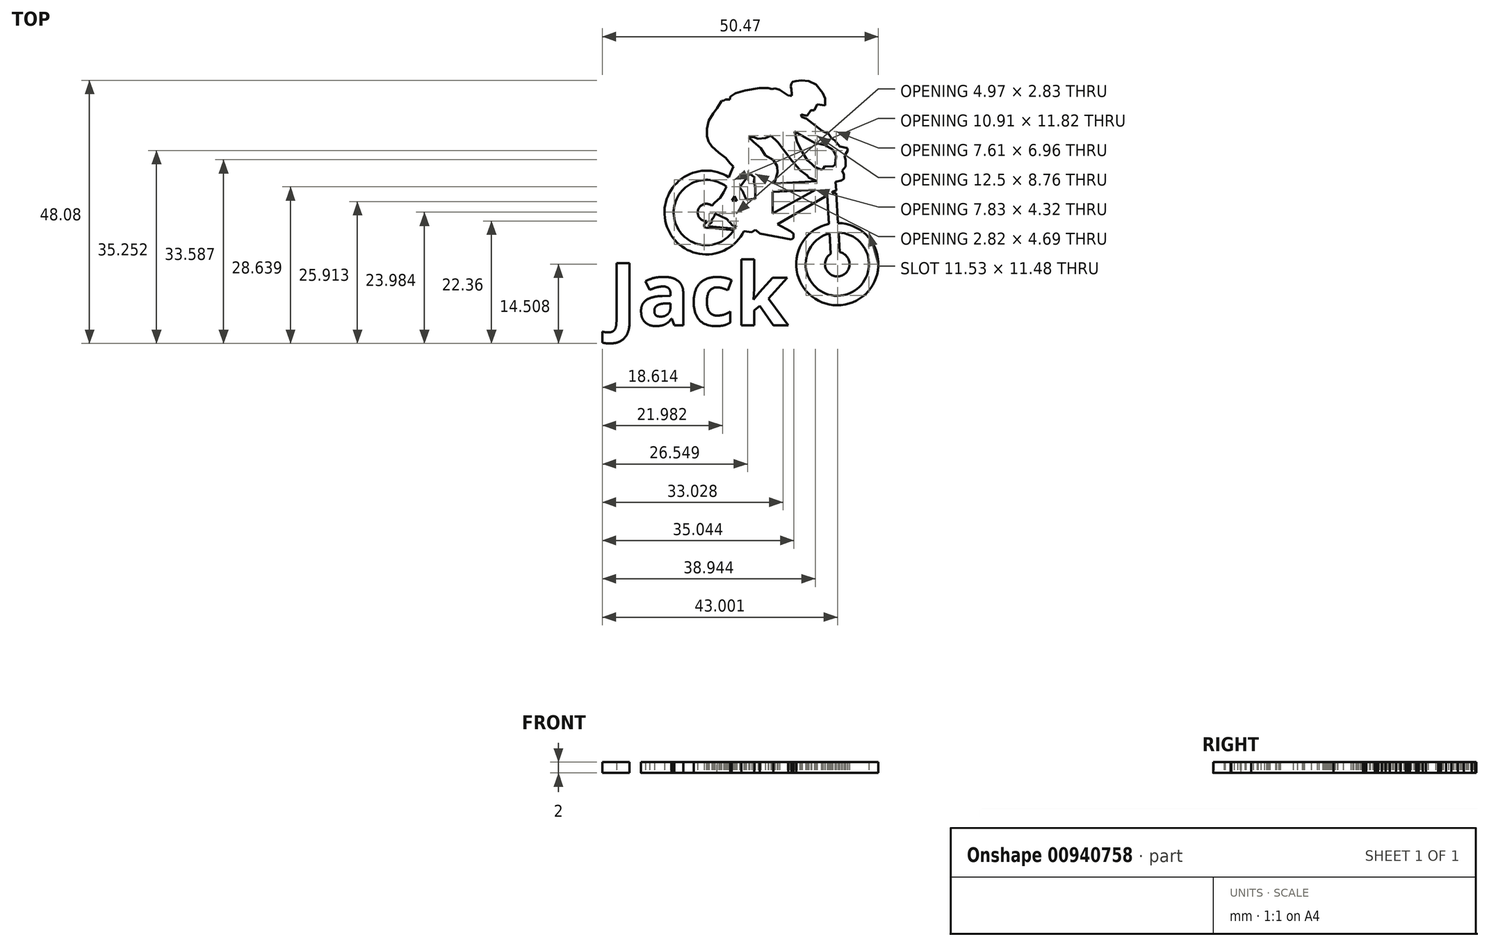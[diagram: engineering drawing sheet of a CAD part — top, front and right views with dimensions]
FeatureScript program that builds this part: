
annotation { "Feature Type Name" : "Feature", "Feature Type Description" : "" }
export const myFeature = defineFeature(function(context is Context, id is Id, definition is map)
    precondition{}
    {
        {
            var Q0;
            Q0=qCreatedBy(makeId("Top.planeOp"),FACE);
            var sketch = newSketch(context, id + "F0", { "sketchPlane" : qUnion([Q0])});
            skArc(sketch, "E0", {"start": v(9.46, 16.17) * mm, "mid": v(9.86, 16.65) * mm, "end": v(10.04, 17.25) * mm});
            skArc(sketch, "E1", {"start": v(31.19, 9.87) * mm, "mid": v(32.78, 5.77) * mm, "end": v(32.82, 10.17) * mm});
            skArc(sketch, "E2", {"start": v(13.63, 14.42) * mm, "mid": v(13.76, 14.68) * mm, "end": v(13.89, 14.94) * mm});
            skArc(sketch, "E3", {"start": v(15.74, 19.77) * mm, "mid": v(0.82, 17.96) * mm, "end": v(15.32, 14.02) * mm});
            skArc(sketch, "E4", {"start": v(30.96, 13.58) * mm, "mid": v(32.98, 2.22) * mm, "end": v(32.6, 13.75) * mm});
            skArc(sketch, "E5", {"start": v(30.86, 15.33) * mm, "mid": v(33.08, 0.5) * mm, "end": v(32.5, 15.49) * mm});
            skLineSegment(sketch, "E6", {"start": v(32.82, 10.17) * mm, "end": v(32.6, 13.75) * mm});
            skLineSegment(sketch, "E7", {"start": v(31.19, 9.87) * mm, "end": v(30.96, 13.58) * mm});
            skLineSegment(sketch, "E8", {"start": v(32.17, 20.9) * mm, "end": v(31.44, 21) * mm});
            skLineSegment(sketch, "E9", {"start": v(31.44, 21) * mm, "end": v(31.46, 21.25) * mm});
            skLineSegment(sketch, "E10", {"start": v(31.46, 21.25) * mm, "end": v(32.17, 21.42) * mm});
            skLineSegment(sketch, "E11", {"start": v(32.17, 21.42) * mm, "end": v(32.07, 23.05) * mm});
            skLineSegment(sketch, "E12", {"start": v(32.07, 23.05) * mm, "end": v(33.13, 23.28) * mm});
            skLineSegment(sketch, "E13", {"start": v(33.13, 23.28) * mm, "end": v(33.58, 23.61) * mm});
            skLineSegment(sketch, "E14", {"start": v(33.58, 23.61) * mm, "end": v(33.58, 24.32) * mm});
            skLineSegment(sketch, "E15", {"start": v(33.58, 24.32) * mm, "end": v(33.27, 25.03) * mm});
            skLineSegment(sketch, "E16", {"start": v(33.27, 25.03) * mm, "end": v(33.92, 25.8) * mm});
            skLineSegment(sketch, "E17", {"start": v(33.92, 25.8) * mm, "end": v(33.92, 26.93) * mm});
            skLineSegment(sketch, "E18", {"start": v(33.92, 26.93) * mm, "end": v(33.73, 27.75) * mm});
            skLineSegment(sketch, "E19", {"start": v(33.73, 27.75) * mm, "end": v(34.26, 28.72) * mm});
            skLineSegment(sketch, "E20", {"start": v(34.26, 28.72) * mm, "end": v(34.2, 29.16) * mm});
            skLineSegment(sketch, "E21", {"start": v(34.2, 29.16) * mm, "end": v(32.8, 29.47) * mm});
            skLineSegment(sketch, "E22", {"start": v(32.8, 29.47) * mm, "end": v(31.94, 30.57) * mm});
            skLineSegment(sketch, "E23", {"start": v(31.94, 30.57) * mm, "end": v(31.27, 31.04) * mm});
            skLineSegment(sketch, "E24", {"start": v(31.27, 31.04) * mm, "end": v(30.78, 31.8) * mm});
            skLineSegment(sketch, "E25", {"start": v(30.78, 31.8) * mm, "end": v(29.59, 32.36) * mm});
            skLineSegment(sketch, "E26", {"start": v(29.59, 32.36) * mm, "end": v(26.7, 34.6) * mm});
            skLineSegment(sketch, "E27", {"start": v(25.76, 35.35) * mm, "end": v(26.88, 35.1) * mm});
            skLineSegment(sketch, "E28", {"start": v(26.88, 35.1) * mm, "end": v(27.53, 36.08) * mm});
            skLineSegment(sketch, "E29", {"start": v(27.53, 36.08) * mm, "end": v(28.17, 36.08) * mm});
            skLineSegment(sketch, "E30", {"start": v(28.17, 36.08) * mm, "end": v(28.69, 37.17) * mm});
            skLineSegment(sketch, "E31", {"start": v(28.69, 37.17) * mm, "end": v(30.13, 37) * mm});
            skLineSegment(sketch, "E32", {"start": v(30.13, 37) * mm, "end": v(30.13, 38.23) * mm});
            skLineSegment(sketch, "E33", {"start": v(30.13, 38.23) * mm, "end": v(29.7, 39.27) * mm});
            skLineSegment(sketch, "E34", {"start": v(29.7, 39.27) * mm, "end": v(28.48, 40.78) * mm});
            skLineSegment(sketch, "E35", {"start": v(28.48, 40.78) * mm, "end": v(27.15, 41.4) * mm});
            skLineSegment(sketch, "E36", {"start": v(27.15, 41.4) * mm, "end": v(25.85, 41.56) * mm});
            skLineSegment(sketch, "E37", {"start": v(25.85, 41.56) * mm, "end": v(24.83, 41.42) * mm});
            skLineSegment(sketch, "E38", {"start": v(24.83, 41.42) * mm, "end": v(24.23, 41.28) * mm});
            skLineSegment(sketch, "E39", {"start": v(24.23, 41.28) * mm, "end": v(24, 40.98) * mm});
            skLineSegment(sketch, "E40", {"start": v(24, 40.98) * mm, "end": v(23.9, 40.5) * mm});
            skLineSegment(sketch, "E41", {"start": v(23.9, 40.5) * mm, "end": v(24, 39.92) * mm});
            skLineSegment(sketch, "E42", {"start": v(24, 39.92) * mm, "end": v(24.07, 39.07) * mm});
            skLineSegment(sketch, "E43", {"start": v(24.07, 39.07) * mm, "end": v(24.07, 38.75) * mm});
            skLineSegment(sketch, "E44", {"start": v(24.07, 38.75) * mm, "end": v(23.73, 38.75) * mm});
            skLineSegment(sketch, "E45", {"start": v(23.73, 38.75) * mm, "end": v(23.35, 38.83) * mm});
            skLineSegment(sketch, "E46", {"start": v(23.35, 38.83) * mm, "end": v(21.85, 39.82) * mm});
            skLineSegment(sketch, "E47", {"start": v(21.85, 39.82) * mm, "end": v(20.99, 40.1) * mm});
            skLineSegment(sketch, "E48", {"start": v(20.99, 40.1) * mm, "end": v(20.46, 39.98) * mm});
            skLineSegment(sketch, "E49", {"start": v(20.46, 39.98) * mm, "end": v(19.7, 40.14) * mm});
            skLineSegment(sketch, "E50", {"start": v(19.7, 40.14) * mm, "end": v(18.17, 40.14) * mm});
            skLineSegment(sketch, "E51", {"start": v(18.17, 40.14) * mm, "end": v(15.53, 39.7) * mm});
            skLineSegment(sketch, "E52", {"start": v(15.53, 39.7) * mm, "end": v(13.8, 39.18) * mm});
            skLineSegment(sketch, "E53", {"start": v(13.8, 39.18) * mm, "end": v(12.83, 38.56) * mm});
            skLineSegment(sketch, "E54", {"start": v(12.83, 38.56) * mm, "end": v(12.72, 38.07) * mm});
            skLineSegment(sketch, "E55", {"start": v(12.72, 38.07) * mm, "end": v(11.93, 38.07) * mm});
            skLineSegment(sketch, "E56", {"start": v(11.93, 38.07) * mm, "end": v(11.65, 37.86) * mm});
            skLineSegment(sketch, "E57", {"start": v(11.65, 37.86) * mm, "end": v(11.2, 37.8) * mm});
            skLineSegment(sketch, "E58", {"start": v(11.2, 37.8) * mm, "end": v(11.04, 37.47) * mm});
            skLineSegment(sketch, "E59", {"start": v(11.04, 37.47) * mm, "end": v(10.4, 36.5) * mm});
            skLineSegment(sketch, "E60", {"start": v(10.4, 36.5) * mm, "end": v(9.7, 35.53) * mm});
            skLineSegment(sketch, "E61", {"start": v(9.7, 35.53) * mm, "end": v(8.86, 34.18) * mm});
            skLineSegment(sketch, "E62", {"start": v(8.86, 34.18) * mm, "end": v(8.55, 32.73) * mm});
            skLineSegment(sketch, "E63", {"start": v(8.55, 32.73) * mm, "end": v(8.55, 31.33) * mm});
            skLineSegment(sketch, "E64", {"start": v(8.55, 31.33) * mm, "end": v(8.86, 30.34) * mm});
            skLineSegment(sketch, "E65", {"start": v(8.86, 30.34) * mm, "end": v(9.42, 29.47) * mm});
            skLineSegment(sketch, "E66", {"start": v(9.42, 29.47) * mm, "end": v(10.7, 28.33) * mm});
            skLineSegment(sketch, "E67", {"start": v(10.7, 28.33) * mm, "end": v(12, 27.38) * mm});
            skLineSegment(sketch, "E68", {"start": v(12, 27.38) * mm, "end": v(12.74, 26.46) * mm});
            skLineSegment(sketch, "E69", {"start": v(12.74, 26.46) * mm, "end": v(13.42, 25.8) * mm});
            skLineSegment(sketch, "E70", {"start": v(13.42, 25.8) * mm, "end": v(12.97, 24.82) * mm});
            skLineSegment(sketch, "E71", {"start": v(12.97, 24.82) * mm, "end": v(12.58, 23.86) * mm});
            skLineSegment(sketch, "E72", {"start": v(12.09, 22.15) * mm, "end": v(11.6, 21.12) * mm});
            skLineSegment(sketch, "E73", {"start": v(11.6, 21.12) * mm, "end": v(10.99, 20.07) * mm});
            skLineSegment(sketch, "E74", {"start": v(10.99, 20.07) * mm, "end": v(9.98, 19.19) * mm});
            skLineSegment(sketch, "E75", {"start": v(9.98, 19.19) * mm, "end": v(9.43, 18.67) * mm});
            skLineSegment(sketch, "E76.trimOffspring", {"start": v(32.5, 15.49) * mm, "end": v(32.17, 20.9) * mm});
            skLineSegment(sketch, "E77.trimOffspring", {"start": v(30.86, 15.33) * mm, "end": v(30.54, 20.52) * mm});
            skLineSegment(sketch, "E78", {"start": v(9.46, 16.17) * mm, "end": v(9.46, 15.66) * mm});
            skLineSegment(sketch, "E79", {"start": v(9.46, 15.66) * mm, "end": v(8.91, 15.2) * mm});
            skLineSegment(sketch, "E80", {"start": v(8.91, 15.2) * mm, "end": v(8.91, 14.87) * mm});
            skLineSegment(sketch, "E81", {"start": v(8.68, 14.66) * mm, "end": v(8.45, 14.57) * mm});
            skLineSegment(sketch, "E82", {"start": v(8.45, 14.57) * mm, "end": v(8.04, 14.8) * mm});
            skLineSegment(sketch, "E83", {"start": v(8.04, 14.8) * mm, "end": v(8.04, 15.29) * mm});
            skLineSegment(sketch, "E84", {"start": v(8.04, 15.29) * mm, "end": v(8.52, 15.58) * mm});
            skLineSegment(sketch, "E85", {"start": v(8.52, 15.58) * mm, "end": v(8.52, 15.82) * mm});
            skLineSegment(sketch, "E86", {"start": v(8.68, 14.66) * mm, "end": v(13.5, 14.2) * mm});
            skLineSegment(sketch, "E87", {"start": v(8.91, 14.87) * mm, "end": v(13.63, 14.42) * mm});
            skLineSegment(sketch, "E88", {"start": v(10.04, 17.25) * mm, "end": v(12.15, 16.22) * mm});
            skLineSegment(sketch, "E89", {"start": v(12.15, 16.22) * mm, "end": v(13.27, 15.03) * mm});
            skLineSegment(sketch, "E90", {"start": v(13.27, 15.03) * mm, "end": v(13.89, 14.94) * mm});
            skArc(sketch, "E91.trimOffspring", {"start": v(9.43, 18.67) * mm, "mid": v(6.94, 17.9) * mm, "end": v(8.52, 15.82) * mm});
            skLineSegment(sketch, "E92", {"start": v(13.62, 20.4) * mm, "end": v(13.12, 19.57) * mm});
            skLineSegment(sketch, "E93", {"start": v(13.12, 19.57) * mm, "end": v(14.02, 19.57) * mm});
            skLineSegment(sketch, "E94", {"start": v(14.38, 18.14) * mm, "end": v(12.44, 18.14) * mm});
            skLineSegment(sketch, "E95", {"start": v(12.44, 18.14) * mm, "end": v(12.5, 17.8) * mm});
            skLineSegment(sketch, "E96", {"start": v(12.58, 17.73) * mm, "end": v(14.33, 16.34) * mm});
            skArc(sketch, "E97.trimOffspring", {"start": v(12.09, 22.15) * mm, "mid": v(2.58, 16.37) * mm, "end": v(13.5, 14.2) * mm});
            skArc(sketch, "E98.trimOffspring", {"start": v(14.33, 16.34) * mm, "mid": v(14.42, 17.23) * mm, "end": v(14.38, 18.14) * mm});
            skArc(sketch, "E99.trimOffspring", {"start": v(14.02, 19.57) * mm, "mid": v(13.84, 20) * mm, "end": v(13.62, 20.4) * mm});
            skLineSegment(sketch, "E100", {"start": v(14.56, 22.03) * mm, "end": v(16.38, 24.46) * mm});
            skLineSegment(sketch, "E101", {"start": v(16.38, 24.46) * mm, "end": v(17.25, 23.81) * mm});
            skLineSegment(sketch, "E102", {"start": v(17.25, 23.81) * mm, "end": v(17.13, 23.07) * mm});
            skLineSegment(sketch, "E103", {"start": v(17.13, 23.07) * mm, "end": v(17.38, 22.19) * mm});
            skLineSegment(sketch, "E104", {"start": v(17.38, 22.19) * mm, "end": v(17.38, 19.9) * mm});
            skLineSegment(sketch, "E105", {"start": v(17.38, 19.9) * mm, "end": v(15.74, 19.77) * mm});
            skLineSegment(sketch, "E106", {"start": v(15.32, 14.02) * mm, "end": v(16.75, 13.83) * mm});
            skLineSegment(sketch, "E107", {"start": v(16.75, 13.83) * mm, "end": v(17.4, 14.28) * mm});
            skLineSegment(sketch, "E108", {"start": v(17.4, 14.28) * mm, "end": v(18.28, 13.53) * mm});
            skLineSegment(sketch, "E109", {"start": v(18.28, 13.53) * mm, "end": v(23.97, 12.48) * mm});
            skLineSegment(sketch, "E110", {"start": v(23.97, 12.48) * mm, "end": v(24.37, 12.8) * mm});
            skLineSegment(sketch, "E111", {"start": v(24.37, 12.8) * mm, "end": v(24.37, 13.53) * mm});
            skLineSegment(sketch, "E112", {"start": v(24.37, 13.53) * mm, "end": v(23.82, 14.02) * mm});
            skLineSegment(sketch, "E113", {"start": v(23.82, 14.02) * mm, "end": v(21.44, 15.3) * mm});
            skLineSegment(sketch, "E114", {"start": v(21.44, 15.3) * mm, "end": v(30.54, 20.52) * mm});
            skLineSegment(sketch, "E115", {"start": v(28.38, 21.55) * mm, "end": v(20.55, 17.23) * mm});
            skLineSegment(sketch, "E116", {"start": v(20.55, 17.23) * mm, "end": v(20.55, 21.2) * mm});
            skLineSegment(sketch, "E117", {"start": v(20.55, 21.2) * mm, "end": v(28.38, 21.55) * mm});
            skLineSegment(sketch, "E118", {"start": v(28.7, 23.16) * mm, "end": v(20.9, 22.69) * mm});
            skPoint(sketch, "E118.startSnap0", {"position": v(32.6, 23.16) * mm});
            skLineSegment(sketch, "E119", {"start": v(20.9, 22.69) * mm, "end": v(21.44, 24.7) * mm});
            skLineSegment(sketch, "E120", {"start": v(21.44, 24.7) * mm, "end": v(21.37, 25.88) * mm});
            skLineSegment(sketch, "E121", {"start": v(21.37, 25.88) * mm, "end": v(20.7, 27.05) * mm});
            skLineSegment(sketch, "E122", {"start": v(20.7, 27.05) * mm, "end": v(19.2, 27.85) * mm});
            skLineSegment(sketch, "E123", {"start": v(19.2, 27.85) * mm, "end": v(18.43, 29.2) * mm});
            skLineSegment(sketch, "E124", {"start": v(18.43, 29.2) * mm, "end": v(17.06, 30.3) * mm});
            skLineSegment(sketch, "E125", {"start": v(17.06, 30.3) * mm, "end": v(16.2, 31.15) * mm});
            skLineSegment(sketch, "E126", {"start": v(16.2, 31.15) * mm, "end": v(17.06, 31.2) * mm});
            skLineSegment(sketch, "E127", {"start": v(17.06, 31.2) * mm, "end": v(17.88, 30.88) * mm});
            skLineSegment(sketch, "E128", {"start": v(17.88, 30.88) * mm, "end": v(19.25, 31.05) * mm});
            skLineSegment(sketch, "E129", {"start": v(19.25, 31.05) * mm, "end": v(20.22, 31.45) * mm});
            skLineSegment(sketch, "E130", {"start": v(20.22, 31.45) * mm, "end": v(21.54, 30.25) * mm});
            skLineSegment(sketch, "E131", {"start": v(21.54, 30.25) * mm, "end": v(24.11, 26.84) * mm});
            skLineSegment(sketch, "E132", {"start": v(24.11, 26.84) * mm, "end": v(25.51, 25.25) * mm});
            skLineSegment(sketch, "E133", {"start": v(25.51, 25.19) * mm, "end": v(26.73, 24.3) * mm});
            skLineSegment(sketch, "E134", {"start": v(26.82, 24.2) * mm, "end": v(27.18, 23.76) * mm});
            skLineSegment(sketch, "E135", {"start": v(27.18, 23.76) * mm, "end": v(28.7, 23.16) * mm});
            skLineSegment(sketch, "E136", {"start": v(26.82, 24.2) * mm, "end": v(26.73, 24.3) * mm});
            skLineSegment(sketch, "E137", {"start": v(25.51, 25.19) * mm, "end": v(25.51, 25.25) * mm});
            skLineSegment(sketch, "E138", {"start": v(24.56, 32.21) * mm, "end": v(25, 30.3) * mm});
            skLineSegment(sketch, "E139", {"start": v(25, 30.3) * mm, "end": v(25.95, 28.48) * mm});
            skLineSegment(sketch, "E140", {"start": v(25.95, 28.48) * mm, "end": v(26.92, 26.94) * mm});
            skLineSegment(sketch, "E141", {"start": v(26.92, 26.94) * mm, "end": v(27.65, 26.3) * mm});
            skLineSegment(sketch, "E142", {"start": v(27.65, 26.3) * mm, "end": v(28.23, 25.74) * mm});
            skLineSegment(sketch, "E143", {"start": v(28.23, 25.74) * mm, "end": v(29.48, 25.25) * mm});
            skLineSegment(sketch, "E144", {"start": v(29.48, 25.25) * mm, "end": v(29.79, 25.4) * mm});
            skLineSegment(sketch, "E145", {"start": v(29.79, 25.4) * mm, "end": v(30.07, 25.9) * mm});
            skLineSegment(sketch, "E146", {"start": v(30.07, 25.9) * mm, "end": v(31.54, 25.84) * mm});
            skLineSegment(sketch, "E147", {"start": v(31.54, 25.84) * mm, "end": v(31.99, 26.2) * mm});
            skLineSegment(sketch, "E148", {"start": v(31.99, 26.2) * mm, "end": v(32.09, 27.04) * mm});
            skLineSegment(sketch, "E149", {"start": v(32.09, 27.04) * mm, "end": v(32.17, 27.71) * mm});
            skLineSegment(sketch, "E150", {"start": v(32.17, 27.71) * mm, "end": v(31.54, 28.9) * mm});
            skLineSegment(sketch, "E151", {"start": v(31.54, 28.9) * mm, "end": v(30.07, 29.74) * mm});
            skLineSegment(sketch, "E152", {"start": v(30.07, 29.74) * mm, "end": v(28.23, 30.13) * mm});
            skLineSegment(sketch, "E153", {"start": v(28.23, 30.13) * mm, "end": v(26.92, 30.87) * mm});
            skLineSegment(sketch, "E154", {"start": v(26.92, 30.87) * mm, "end": v(24.56, 32.21) * mm});
            skLineSegment(sketch, "E155", {"start": v(26.7, 34.6) * mm, "end": v(25.84, 34.9) * mm});
            skLineSegment(sketch, "E156", {"start": v(25.76, 35.35) * mm, "end": v(25.84, 34.9) * mm});
            skSolve(sketch);
        }
        {
            var Q0;
            Q0=makeQuery(id+"F0.imprint","IMPRINT",FACE,{"disambiguationData":[TD([[makeQuery(id+"F0.imprint","IMPRINT",EDGE,{"derivedFrom":sQuery(id+"F0.wireOp",EDGE,"E0")}),1.0]])]});
            extrude(context, id + "F1", {"entities" : qUnion([Q0]), "depth" : 2 * mm, "offsetDistance" : 25 * mm});
        }
        {
            var Q0;
            Q0=qCreatedBy(makeId("Top.planeOp"), FACE);
            var sketch = newSketch(context, id + "F2", { "sketchPlane" : qUnion([Q0])});
            skText(sketch, "E157", { "text": "Jack", "fontName": "OpenSans-Bold.ttf"});
            const initialGuessF2  = {"E157": [-0.0094, -0.00319, 1, 0, 0.01142]};
            skSetInitialGuess(sketch, initialGuessF2);
            skSolve(sketch);
        }
        {
            var Q0;
            Q0 = qSketchRegion(id + "F2", true);
            extrude(context, id + "F3", {"entities" : qUnion([Q0]), "domain" : OperationDomain.MODEL, "flatOperationType" : FlatOperationType.REMOVE, "depth" : 2 * mm, "offsetDistance" : 25 * mm});
        }
    });
